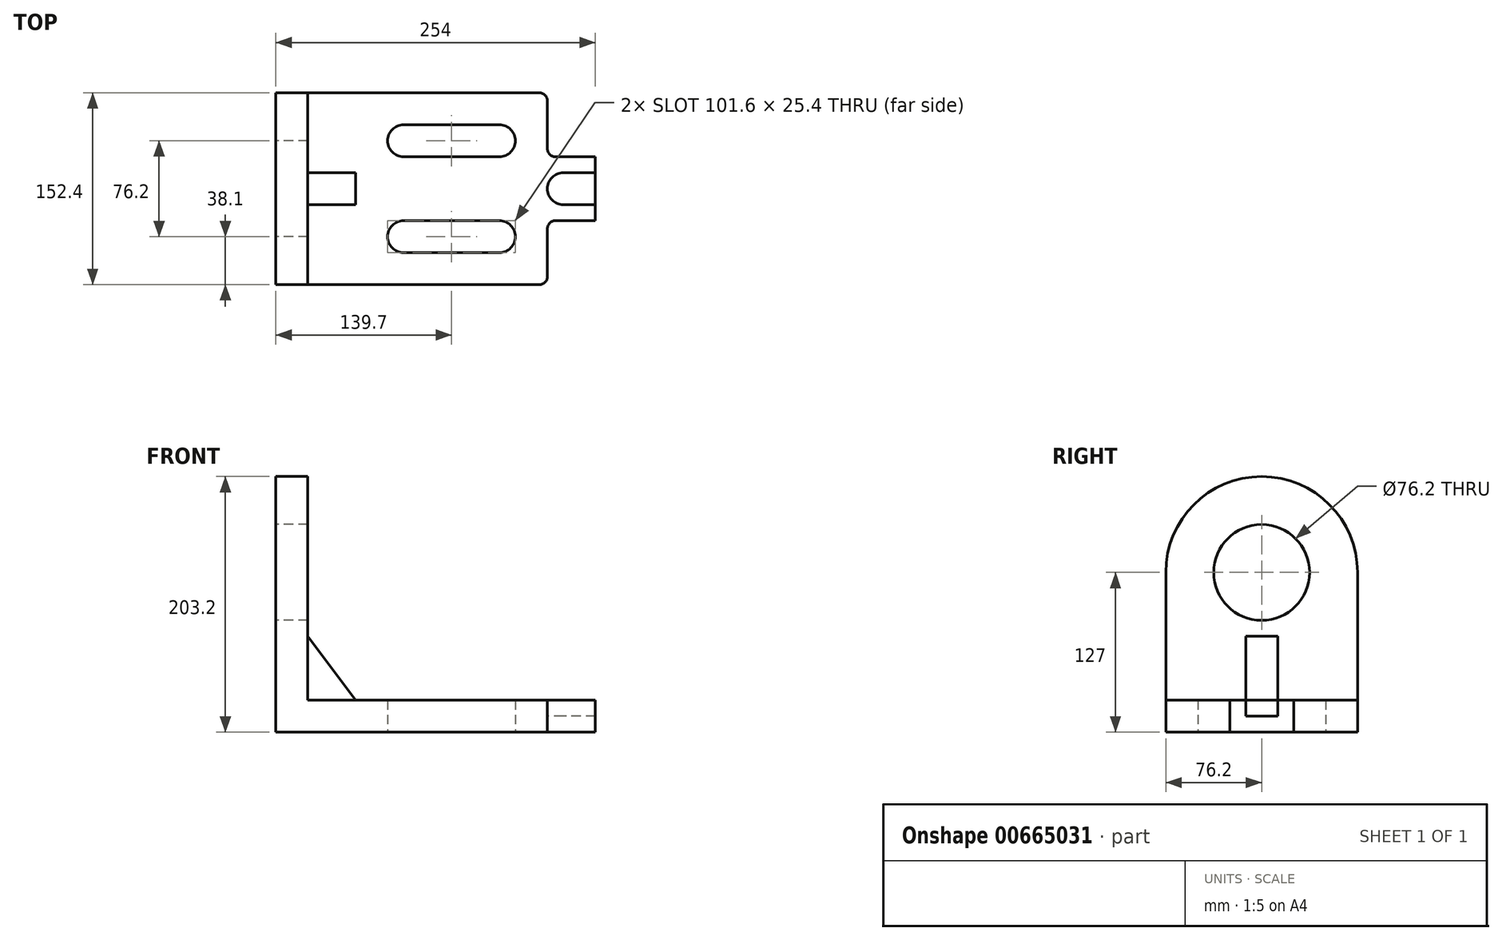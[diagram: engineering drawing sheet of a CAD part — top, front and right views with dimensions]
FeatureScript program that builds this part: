
annotation { "Feature Type Name" : "Feature", "Feature Type Description" : "" }
export const myFeature = defineFeature(function(context is Context, id is Id, definition is map)
    precondition{}
    {
        {
            var Q0;
            Q0=qCreatedBy(makeId("Top.planeOp"),FACE);
            var sketch = newSketch(context, id + "F0", { "sketchPlane" : qUnion([Q0])});
            skLineSegment(sketch, "E0", {"start": v(0, 0) * mm, "end": v(209.55, 0) * mm});
            skLineSegment(sketch, "E1", {"start": v(215.9, 6.35) * mm, "end": v(215.9, 44.45) * mm});
            skLineSegment(sketch, "E2", {"start": v(222.25, 50.8) * mm, "end": v(254, 50.8) * mm});
            skLineSegment(sketch, "E3", {"start": v(254, 50.8) * mm, "end": v(254, 63.5) * mm});
            skLineSegment(sketch, "E4", {"start": v(254, 63.5) * mm, "end": v(228.6, 63.5) * mm});
            skLineSegment(sketch, "E5", {"start": v(215.9, 76.2) * mm, "end": v(215.9, 76.2) * mm});
            skLineSegment(sketch, "E6", {"start": v(228.6, 88.9) * mm, "end": v(254, 88.9) * mm});
            skLineSegment(sketch, "E7", {"start": v(254, 88.9) * mm, "end": v(254, 101.6) * mm});
            skLineSegment(sketch, "E8", {"start": v(254, 101.6) * mm, "end": v(222.25, 101.6) * mm});
            skLineSegment(sketch, "E9", {"start": v(215.9, 107.95) * mm, "end": v(215.9, 146.05) * mm});
            skLineSegment(sketch, "E10", {"start": v(209.55, 152.4) * mm, "end": v(0, 152.4) * mm});
            skLineSegment(sketch, "E11", {"start": v(0, 152.4) * mm, "end": v(0, 0) * mm});
            skPoint(sketch, "E12.visualSharp", {"position": v(215.9, 152.4) * mm});
            skArc(sketch, "E12.filletArc", {"start": v(215.9, 146.05) * mm, "mid": v(214.04, 150.54) * mm, "end": v(209.55, 152.4) * mm});
            skPoint(sketch, "E13.visualSharp", {"position": v(215.9, 0) * mm});
            skArc(sketch, "E13.filletArc", {"start": v(209.55, 0) * mm, "mid": v(214.04, 1.86) * mm, "end": v(215.9, 6.35) * mm});
            skPoint(sketch, "E14.visualSharp", {"position": v(215.9, 50.8) * mm});
            skArc(sketch, "E14.filletArc", {"start": v(222.25, 50.8) * mm, "mid": v(217.76, 48.94) * mm, "end": v(215.9, 44.45) * mm});
            skPoint(sketch, "E15.visualSharp", {"position": v(215.9, 63.5) * mm});
            skArc(sketch, "E15.filletArc", {"start": v(215.9, 76.2) * mm, "mid": v(219.62, 67.22) * mm, "end": v(228.6, 63.5) * mm});
            skPoint(sketch, "E16.visualSharp", {"position": v(215.9, 88.9) * mm});
            skArc(sketch, "E16.filletArc", {"start": v(228.6, 88.9) * mm, "mid": v(219.62, 85.18) * mm, "end": v(215.9, 76.2) * mm});
            skPoint(sketch, "E17.visualSharp", {"position": v(215.9, 101.6) * mm});
            skArc(sketch, "E17.filletArc", {"start": v(215.9, 107.95) * mm, "mid": v(217.76, 103.46) * mm, "end": v(222.25, 101.6) * mm});
            skLineSegment(sketch, "E18", {"start": v(254, 88.9) * mm, "end": v(254, 63.5) * mm});
            skLineSegment(sketch, "E19", {"start": v(0, 152.4) * mm, "end": v(101.6, 152.4) * mm});
            skLineSegment(sketch, "E20", {"start": v(101.6, 152.4) * mm, "end": v(101.6, 114.3) * mm});
            skLineSegment(sketch, "E21", {"start": v(101.6, 114.3) * mm, "end": v(177.8, 114.3) * mm});
            skLineSegment(sketch, "E22", {"start": v(101.6, 114.3) * mm, "end": v(101.6, 127) * mm});
            skCircle(sketch, "E23", {"center": v(101.6, 114.3) * mm, "radius": 12.7 * mm});
            skCircle(sketch, "E24", {"center": v(177.8, 114.3) * mm, "radius": 12.7 * mm});
            skLineSegment(sketch, "E25", {"start": v(177.8, 114.3) * mm, "end": v(177.8, 127) * mm});
            skLineSegment(sketch, "E26", {"start": v(177.8, 127) * mm, "end": v(101.6, 127) * mm});
            skLineSegment(sketch, "E27", {"start": v(101.6, 114.3) * mm, "end": v(101.6, 101.6) * mm});
            skLineSegment(sketch, "E28", {"start": v(101.6, 101.6) * mm, "end": v(177.8, 101.6) * mm});
            skLineSegment(sketch, "E29", {"start": v(177.8, 101.6) * mm, "end": v(177.8, 114.3) * mm});
            skLineSegment(sketch, "E30", {"start": v(0, 0) * mm, "end": v(101.6, 0) * mm});
            skLineSegment(sketch, "E31", {"start": v(101.6, 0) * mm, "end": v(101.6, 38.1) * mm});
            skLineSegment(sketch, "E32", {"start": v(101.6, 38.1) * mm, "end": v(177.8, 38.1) * mm});
            skLineSegment(sketch, "E33", {"start": v(177.8, 38.1) * mm, "end": v(177.8, 25.4) * mm});
            skLineSegment(sketch, "E34", {"start": v(177.8, 38.1) * mm, "end": v(177.8, 50.8) * mm});
            skLineSegment(sketch, "E35", {"start": v(177.8, 50.8) * mm, "end": v(101.6, 50.8) * mm});
            skLineSegment(sketch, "E36", {"start": v(177.8, 25.4) * mm, "end": v(101.6, 25.4) * mm});
            skCircle(sketch, "E37", {"center": v(101.6, 38.1) * mm, "radius": 12.7 * mm});
            skCircle(sketch, "E38", {"center": v(177.8, 38.1) * mm, "radius": 12.7 * mm});
            skSolve(sketch);
        }
        {
            var Q0;
            Q0=makeQuery(id+"F0.imprint","IMPRINT",FACE,{"disambiguationData":[TD([[makeQuery(id+"F0.imprint","IMPRINT",EDGE,{"derivedFrom":sQuery(id+"F0.wireOp",EDGE,"E0")}),1.0]])]});
            extrude(context, id + "F1", {"entities" : qUnion([Q0]), "endBound" : BoundingType.SYMMETRIC, "depth" : 25.4 * mm, "offsetDistance" : 25.4 * mm});
        }
        {
            var Q0;
            Q0=makeQuery(id+"F0.imprint","IMPRINT",FACE,{"disambiguationData":[TD([[makeQuery(id+"F0.imprint","IMPRINT",EDGE,{"derivedFrom":sQuery(id+"F0.wireOp",EDGE,"E4")}),-1.0]])]});
            extrude(context, id + "F2", {"entities" : qUnion([Q0]), "operationType" : NewBodyOperationType.ADD, "oppositeDirection" : true, "depth" : 12.7 * mm, "offsetDistance" : 25.4 * mm});
        }
        {
            var Q0;
            Q0=makeQuery(id+"F1.opExtrude","SWEPT_FACE",FACE,{"disambiguationData":[OSD([sQuery(id+"F0.wireOp",EDGE,"E11")])]});
            var sketch = newSketch(context, id + "F3", { "sketchPlane" : qUnion([Q0])});
            skLineSegment(sketch, "E39", {"start": v(0, 12.7) * mm, "end": v(0, 114.3) * mm});
            skLineSegment(sketch, "E40", {"start": v(-76.2, 190.5) * mm, "end": v(-76.2, 190.5) * mm});
            skLineSegment(sketch, "E41", {"start": v(-152.4, 114.3) * mm, "end": v(-152.4, 12.7) * mm});
            skPoint(sketch, "E42.visualSharp", {"position": v(-152.4, 190.5) * mm});
            skArc(sketch, "E42.filletArc", {"start": v(-76.2, 190.5) * mm, "mid": v(-130.08, 168.18) * mm, "end": v(-152.4, 114.3) * mm});
            skPoint(sketch, "E43.visualSharp", {"position": v(0, 190.5) * mm});
            skArc(sketch, "E43.filletArc", {"start": v(0, 114.3) * mm, "mid": v(-22.32, 168.18) * mm, "end": v(-76.2, 190.5) * mm});
            skCircle(sketch, "E44", {"center": v(-76.2, 114.3) * mm, "radius": 38.1 * mm});
            skSolve(sketch);
        }
        {
            var Q0;
            Q0=makeQuery(id+"F3.imprint","IMPRINT",FACE,{"disambiguationData":[TD([[makeQuery(id+"F3.imprint","IMPRINT",EDGE,{"derivedFrom":sQuery(id+"F3.wireOp",EDGE,"E39")}),1.0]])]});
            extrude(context, id + "F4", {"entities" : qUnion([Q0]), "operationType" : NewBodyOperationType.ADD, "oppositeDirection" : true, "depth" : 25.4 * mm, "offsetDistance" : 25.4 * mm});
        }
        {
            var Q0;
            Q0=makeQuery(id+"F4.boolean.opBoolean","MERGE",FACE,{"derivedFrom":[makeQuery(id+"F1.opExtrude","SWEPT_FACE",FACE,{"disambiguationData":[OSD([sQuery(id+"F0.wireOp",EDGE,"E0"),sQuery(id+"F0.wireOp",EDGE,"E30")])]}),makeQuery(id+"F4.opExtrude","SWEPT_FACE",FACE,{"disambiguationData":[OSD([sQuery(id+"F3.wireOp",EDGE,"E39")])]})]});
            var sketch = newSketch(context, id + "F5", { "sketchPlane" : qUnion([Q0])});
            skLineSegment(sketch, "E45", {"start": v(25.4, 12.7) * mm, "end": v(25.4, 63.5) * mm});
            skLineSegment(sketch, "E46", {"start": v(25.4, 12.7) * mm, "end": v(63.5, 12.7) * mm});
            skLineSegment(sketch, "E47", {"start": v(63.5, 12.7) * mm, "end": v(25.4, 63.5) * mm});
            skSolve(sketch);
        }
        {
            var Q0;
            Q0=makeQuery(id+"F5.imprint","IMPRINT",FACE,{"disambiguationData":[TD([[makeQuery(id+"F5.imprint","IMPRINT",EDGE,{"derivedFrom":sQuery(id+"F5.wireOp",EDGE,"E45")}),-1.0]])]});
            extrude(context, id + "F6", {"entities" : qUnion([Q0]), "operationType" : NewBodyOperationType.ADD, "oppositeDirection" : true, "depth" : 88.9 * mm, "offsetDistance" : 25.4 * mm, "hasSecondDirection" : true, "secondDirectionOppositeDirection" : true, "secondDirectionDepth" : 63.5 * mm});
        }
    });
